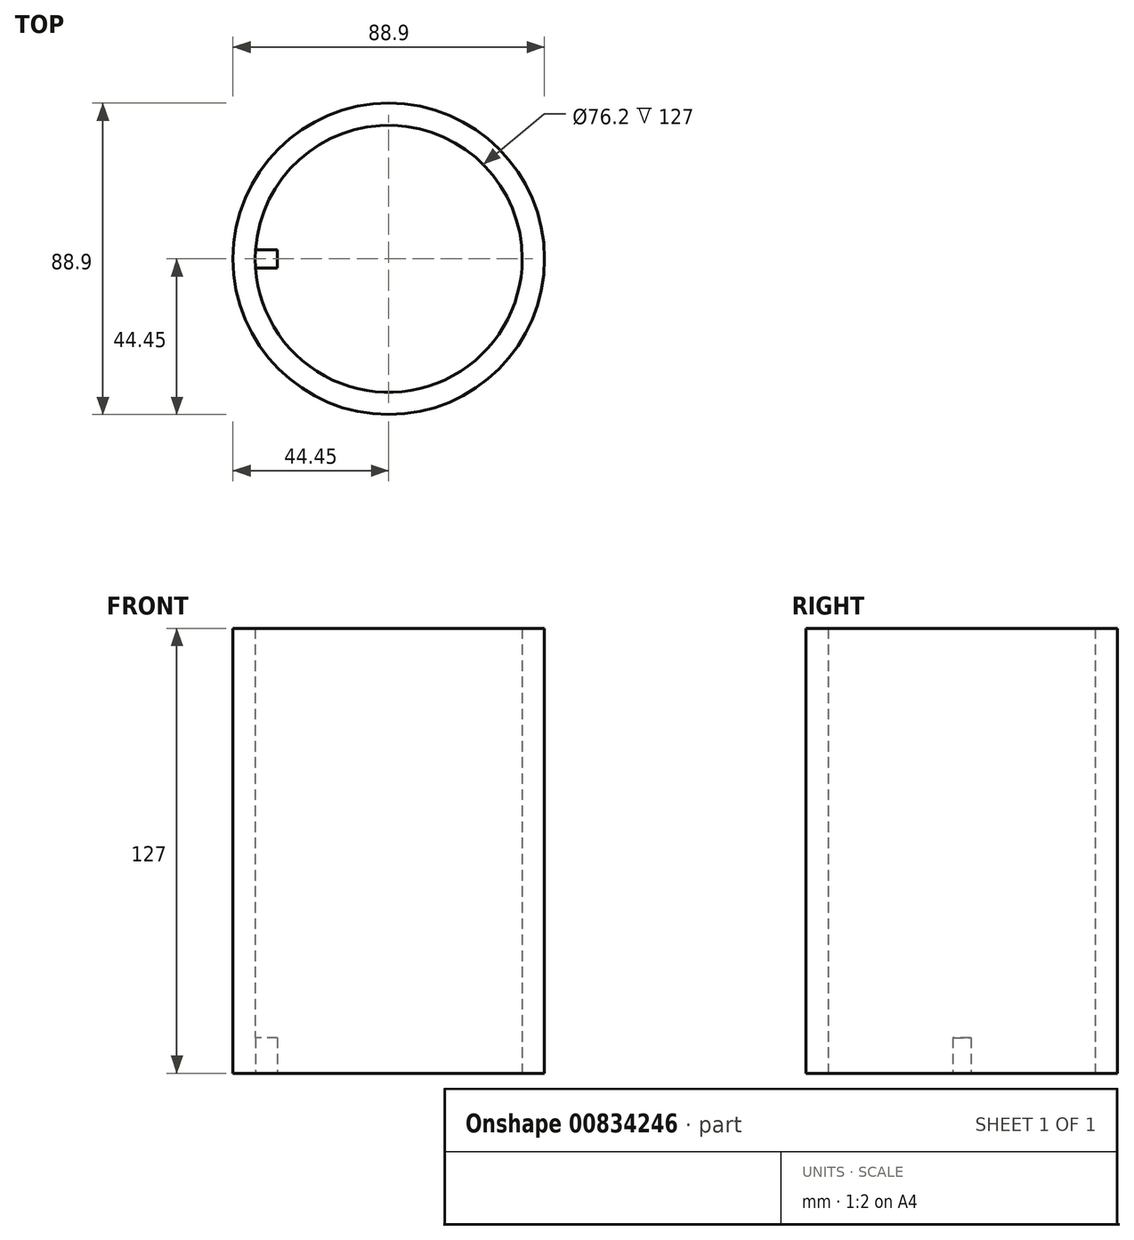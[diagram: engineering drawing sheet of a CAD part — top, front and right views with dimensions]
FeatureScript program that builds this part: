
annotation { "Feature Type Name" : "Feature", "Feature Type Description" : "" }
export const myFeature = defineFeature(function(context is Context, id is Id, definition is map)
    precondition{}
    {
        {
            var Q0;
            Q0=qCreatedBy(makeId("Top.planeOp"),FACE);
            var sketch = newSketch(context, id + "F0", { "sketchPlane" : qUnion([Q0])});
            skCircle(sketch, "E0", {"center": v(0, 0) * mm, "radius": 38.1 * mm});
            skCircle(sketch, "E1", {"center": v(0, 0) * mm, "radius": 44.45 * mm});
            skSolve(sketch);
        }
        {
            var Q0;
            Q0=makeQuery(id+"F0.imprint","IMPRINT",FACE,{"disambiguationData":[TD([[makeQuery(id+"F0.imprint","IMPRINT",EDGE,{"derivedFrom":sQuery(id+"F0.wireOp",EDGE,"E0")}),-1.0]])]});
            var Q1;
            Q1=sQuery(id+"F0.wireOp",EDGE,"E0");
            var Q2;
            Q2=sQuery(id+"F0.wireOp",EDGE,"E1");
            extrude(context, id + "F1", {"entities" : qUnion([Q0]), "surfaceEntities" : qUnion([Q1, Q2]), "depth" : 127 * mm, "offsetDistance" : 25.4 * mm});
        }
        {
            var Q0;
            Q0=qCreatedBy(makeId("Top.planeOp"),FACE);
            var sketch = newSketch(context, id + "F2", { "sketchPlane" : qUnion([Q0])});
            skLineSegment(sketch, "E2.bottom", {"start": v(-31.75, -2.58) * mm, "end": v(-38.1, -2.58) * mm});
            skLineSegment(sketch, "E2.top", {"start": v(-31.75, 2.58) * mm, "end": v(-38.1, 2.58) * mm});
            skLineSegment(sketch, "E2.left", {"start": v(-31.75, -2.58) * mm, "end": v(-31.75, 2.58) * mm});
            skLineSegment(sketch, "E2.right", {"start": v(-38.1, -2.58) * mm, "end": v(-38.1, 2.58) * mm});
            skPoint(sketch, "E2.middle", {"position": v(-34.92, 0) * mm});
            skSolve(sketch);
        }
        {
            var Q0;
            Q0 = qSketchRegion(id + "F2", true);
            extrude(context, id + "F3", {"entities" : qUnion([Q0]), "operationType" : NewBodyOperationType.ADD, "depth" : 10.16 * mm, "offsetDistance" : 25.4 * mm});
        }
    });
